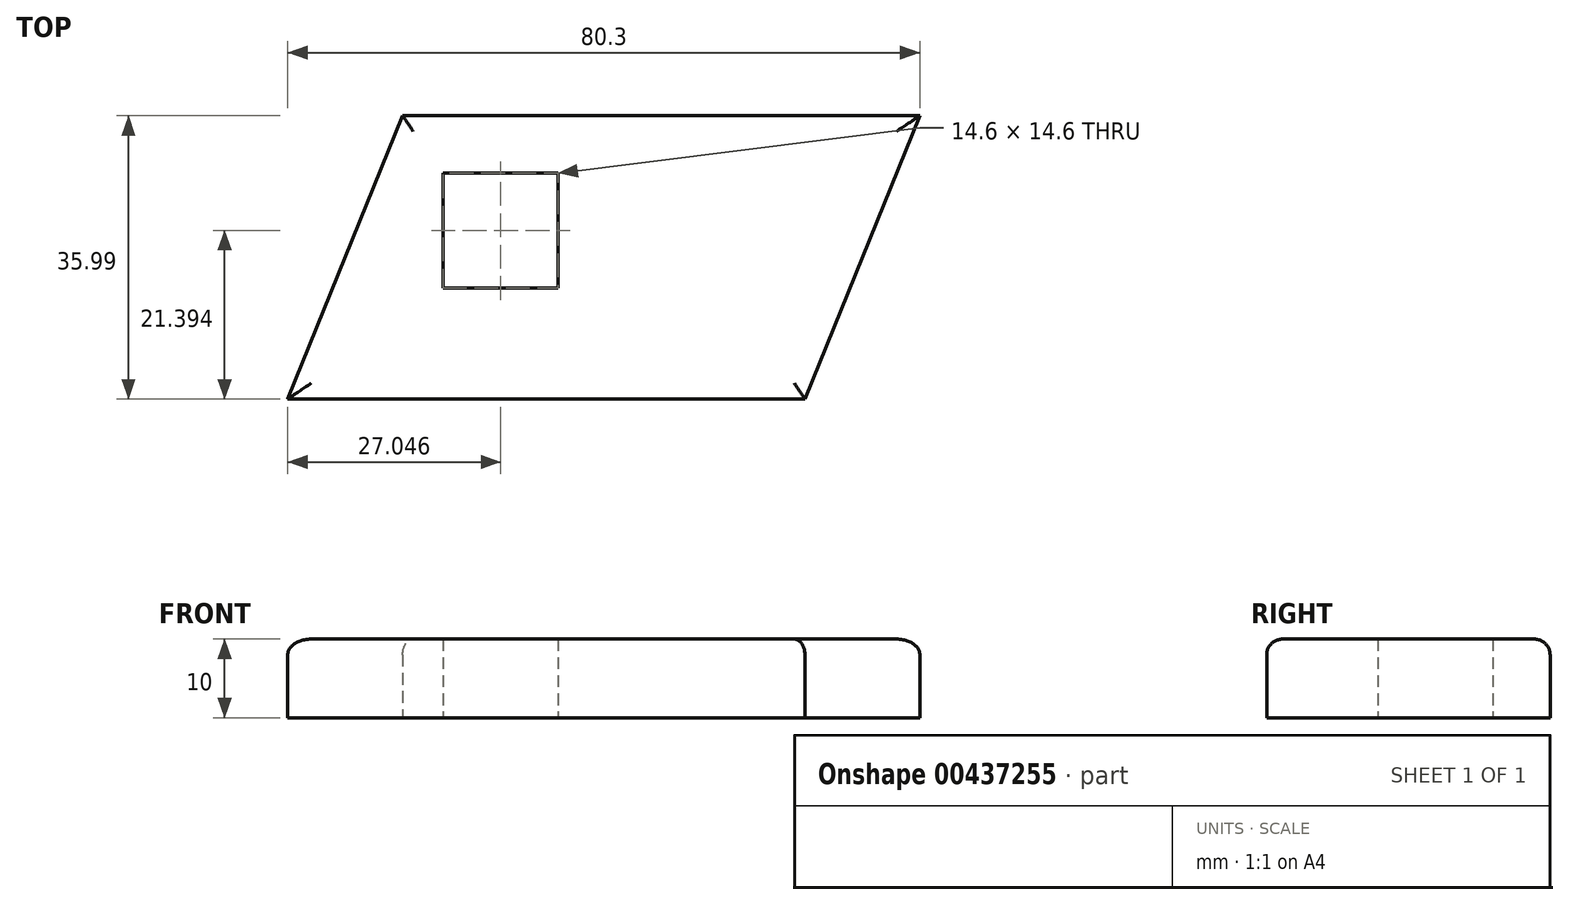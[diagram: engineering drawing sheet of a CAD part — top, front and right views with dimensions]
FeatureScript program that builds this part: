
annotation { "Feature Type Name" : "Feature", "Feature Type Description" : "" }
export const myFeature = defineFeature(function(context is Context, id is Id, definition is map)
    precondition{}
    {
        {
            var Q0;
            Q0=qCreatedBy(makeId("Top.planeOp"),FACE);
            var sketch = newSketch(context, id + "F0", { "sketchPlane" : qUnion([Q0])});
            skLineSegment(sketch, "E0.bottom", {"start": v(-23.72, 23.12) * mm, "end": v(27.38, 23.12) * mm});
            skLineSegment(sketch, "E0.top", {"start": v(-23.72, -12.87) * mm, "end": v(27.38, -12.87) * mm});
            skLineSegment(sketch, "E0.left", {"start": v(-23.72, 23.12) * mm, "end": v(-23.72, -12.87) * mm});
            skLineSegment(sketch, "E0.right", {"start": v(27.38, 23.12) * mm, "end": v(27.38, -12.87) * mm});
            skLineSegment(sketch, "E1", {"start": v(27.38, 23.12) * mm, "end": v(41.98, 23.12) * mm});
            skLineSegment(sketch, "E2", {"start": v(41.98, 23.12) * mm, "end": v(27.38, -12.87) * mm});
            skLineSegment(sketch, "E3", {"start": v(-23.72, -12.87) * mm, "end": v(-38.32, -12.87) * mm});
            skLineSegment(sketch, "E4", {"start": v(-38.32, -12.87) * mm, "end": v(-23.72, 23.12) * mm});
            skLineSegment(sketch, "E5.bottom", {"start": v(-18.57, 15.82) * mm, "end": v(-3.97, 15.82) * mm});
            skLineSegment(sketch, "E5.top", {"start": v(-18.57, 1.22) * mm, "end": v(-3.97, 1.22) * mm});
            skLineSegment(sketch, "E5.left", {"start": v(-18.57, 15.82) * mm, "end": v(-18.57, 1.22) * mm});
            skLineSegment(sketch, "E5.right", {"start": v(-3.97, 15.82) * mm, "end": v(-3.97, 1.22) * mm});
            skSolve(sketch);
        }
        {
            var Q0;
            Q0=makeQuery(id+"F0.imprint","IMPRINT",FACE,{"disambiguationData":[TD([[makeQuery(id+"F0.imprint","IMPRINT",EDGE,{"derivedFrom":sQuery(id+"F0.wireOp",EDGE,"E0.left")}),-1.0]])]});
            var Q1;
            Q1=makeQuery(id+"F0.imprint","IMPRINT",FACE,{"disambiguationData":[TD([[makeQuery(id+"F0.imprint","IMPRINT",EDGE,{"derivedFrom":sQuery(id+"F0.wireOp",EDGE,"E0.bottom")}),-1.0]])]});
            var Q2;
            Q2=makeQuery(id+"F0.imprint","IMPRINT",FACE,{"disambiguationData":[TD([[makeQuery(id+"F0.imprint","IMPRINT",EDGE,{"derivedFrom":sQuery(id+"F0.wireOp",EDGE,"E0.right")}),1.0]])]});
            extrude(context, id + "F1", {"entities" : qUnion([Q0, Q1, Q2]), "depth" : 10 * mm});
        }
        {
            var Q0;
            Q0=makeQuery(id+"F1.opExtrude","CAP_EDGE",EDGE,{"disambiguationData":[OSD([sQuery(id+"F0.wireOp",EDGE,"E0.top"),sQuery(id+"F0.wireOp",EDGE,"E3")])],"isStart":false});
            var Q1;
            Q1=makeQuery(id+"F1.opExtrude","CAP_EDGE",EDGE,{"disambiguationData":[OSD([sQuery(id+"F0.wireOp",EDGE,"E4")])],"isStart":false});
            var Q2;
            Q2=makeQuery(id+"F1.opExtrude","CAP_EDGE",EDGE,{"disambiguationData":[OSD([sQuery(id+"F0.wireOp",EDGE,"E0.bottom"),sQuery(id+"F0.wireOp",EDGE,"E1")])],"isStart":false});
            var Q3;
            Q3=makeQuery(id+"F1.opExtrude","CAP_EDGE",EDGE,{"disambiguationData":[OSD([sQuery(id+"F0.wireOp",EDGE,"E2")])],"isStart":false});
            fillet(context, id + "F2", {"entities" : qUnion([Q0, Q1, Q2, Q3]), "radius" : 2 * mm, "tangentPropagation" : true, "allowEdgeOverflow" : false});
        }
    });
